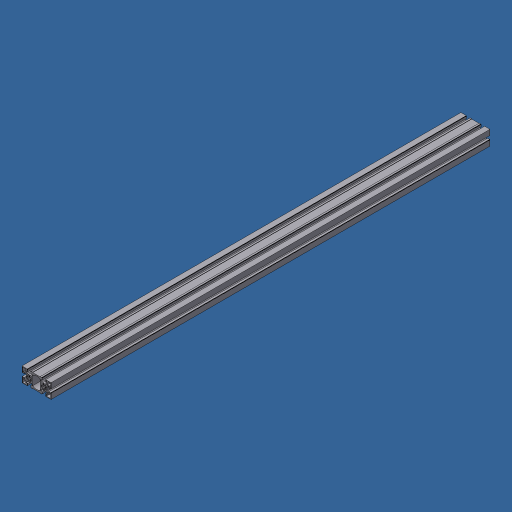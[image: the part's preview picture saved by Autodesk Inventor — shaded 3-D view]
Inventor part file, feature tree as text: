
AUTODESK INVENTOR PART (.ipt)
format: ipt  version: 2024.3 (Build 283343000, 343)  size: 538,112 bytes
history: native  units: mm (DEFAULTED — no unit token found)
features: extrude x2, sketch x2, other x1, hole x1
ambient origin geometry x8: Origin, YZ Plane, XZ Plane, XY Plane, X Axis, Y Axis, Z Axis, Center Point
bodies: Body1 (feature_tree)
feature tree (6):
  other  "Finish - None"
  extrude  "BOSCH, 45X90"  Depth=160.0mm TaperAngle=360.0deg
  extrude  "Extrusion2"  Depth=10.0mm
  hole  "Hole5"  [1 undecoded]
  sketch  "Sketch1"  dims[d0=22.5deg d2=160.0mm d4=360.0deg]
  sketch  "Sketch7"  dims[d6=20.0mm d7=5.0mm d8=8.0mm d9=9.5mm d10=9.5mm d11=9.5mm d13=10.0mm d14=10.0mm d16=10.0mm d21=5.0mm d22=5.0mm d24=22.5mm d26=6.0mm d27=6.0mm d28=1.0mm d29=1.0mm d32=40.0mm d34=360.0deg d36=45.0mm d37=45.0mm d38=10.0mm d39=10.0mm d40=1360.0mm d41=0.0mm d42=45.0deg d44=40.0mm d45=1.9558mm d46=1.9558mm d47=25.4mm d48=0.0mm d49=18.0mm d50=18.0mm d110=450.0mm d111=225.0mm d112=22.5mm d113=45.0mm d114=9.0mm d115=12.7mm d116=9.525mm d117=6.35mm d118=14.3117mm d119=19.05mm d120=20.594885mm]
note: 1 required parameter value undecoded (feature->parameter linkage not recoverable at this tier; creation-order binding heuristic only, values carry confidence <= 0.55)
